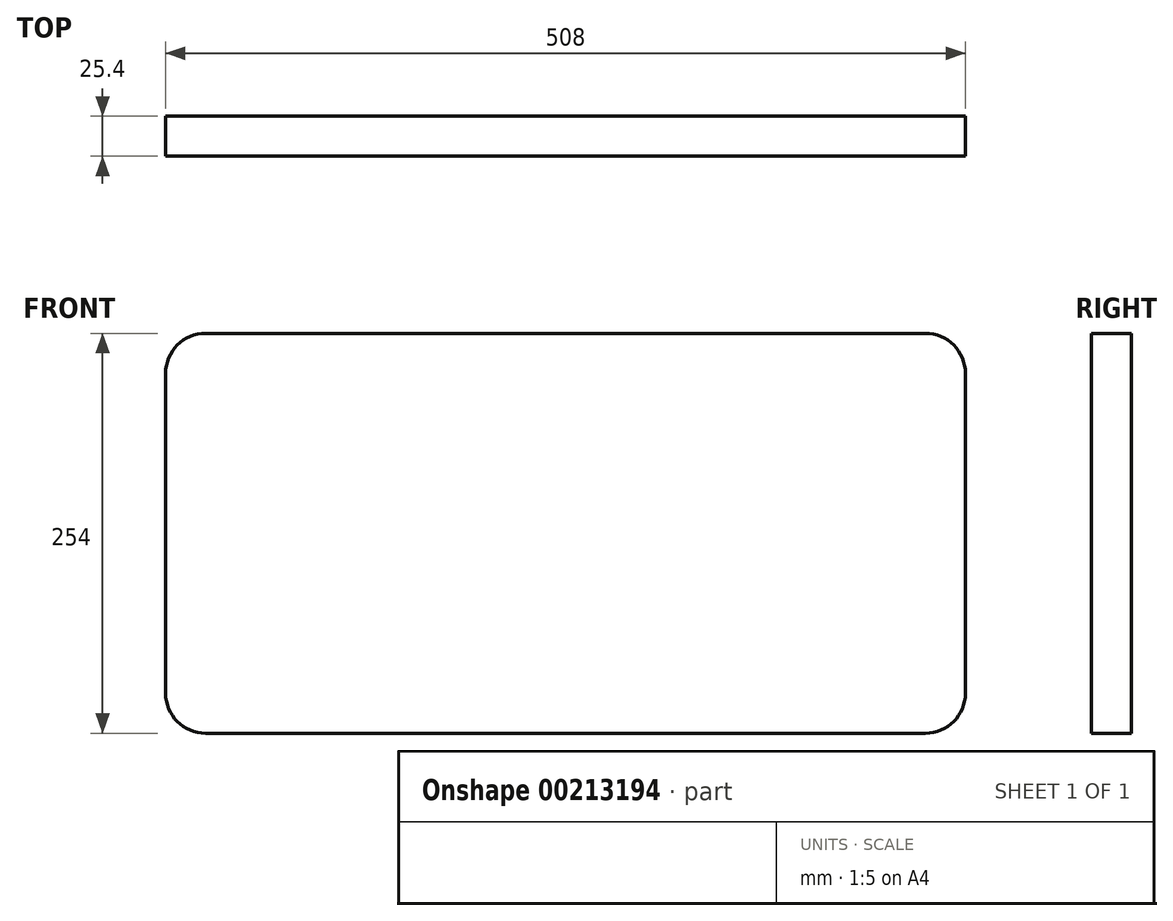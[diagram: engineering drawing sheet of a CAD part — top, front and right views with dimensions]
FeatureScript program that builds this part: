
annotation { "Feature Type Name" : "Feature", "Feature Type Description" : "" }
export const myFeature = defineFeature(function(context is Context, id is Id, definition is map)
    precondition{}
    {
        {
            var Q0;
            Q0=qCreatedBy(makeId("Front.planeOp"),FACE);
            var sketch = newSketch(context, id + "F0", { "sketchPlane" : qUnion([Q0])});
            skLineSegment(sketch, "E0.bottom", {"start": v(25.4, 0) * mm, "end": v(482.6, 0) * mm});
            skLineSegment(sketch, "E0.top", {"start": v(25.4, -254) * mm, "end": v(482.6, -254) * mm});
            skLineSegment(sketch, "E0.left", {"start": v(0, -25.4) * mm, "end": v(0, -228.6) * mm});
            skLineSegment(sketch, "E0.right", {"start": v(508, -25.4) * mm, "end": v(508, -228.6) * mm});
            skPoint(sketch, "E1.visualSharp", {"position": v(0, -254) * mm});
            skArc(sketch, "E1.filletArc", {"start": v(0, -228.6) * mm, "mid": v(7.44, -246.56) * mm, "end": v(25.4, -254) * mm});
            skPoint(sketch, "E2.visualSharp", {"position": v(0, 0) * mm});
            skArc(sketch, "E2.filletArc", {"start": v(25.4, 0) * mm, "mid": v(7.44, -7.44) * mm, "end": v(0, -25.4) * mm});
            skPoint(sketch, "E3.visualSharp", {"position": v(508, 0) * mm});
            skArc(sketch, "E3.filletArc", {"start": v(508, -25.4) * mm, "mid": v(500.56, -7.44) * mm, "end": v(482.6, 0) * mm});
            skPoint(sketch, "E4.visualSharp", {"position": v(508, -254) * mm});
            skArc(sketch, "E4.filletArc", {"start": v(482.6, -254) * mm, "mid": v(500.56, -246.56) * mm, "end": v(508, -228.6) * mm});
            skSolve(sketch);
        }
        {
            var Q0;
            Q0 = qSketchRegion(id + "F0", true);
            extrude(context, id + "F1", {"entities" : qUnion([Q0]), "depth" : 25.4 * mm});
        }
    });
